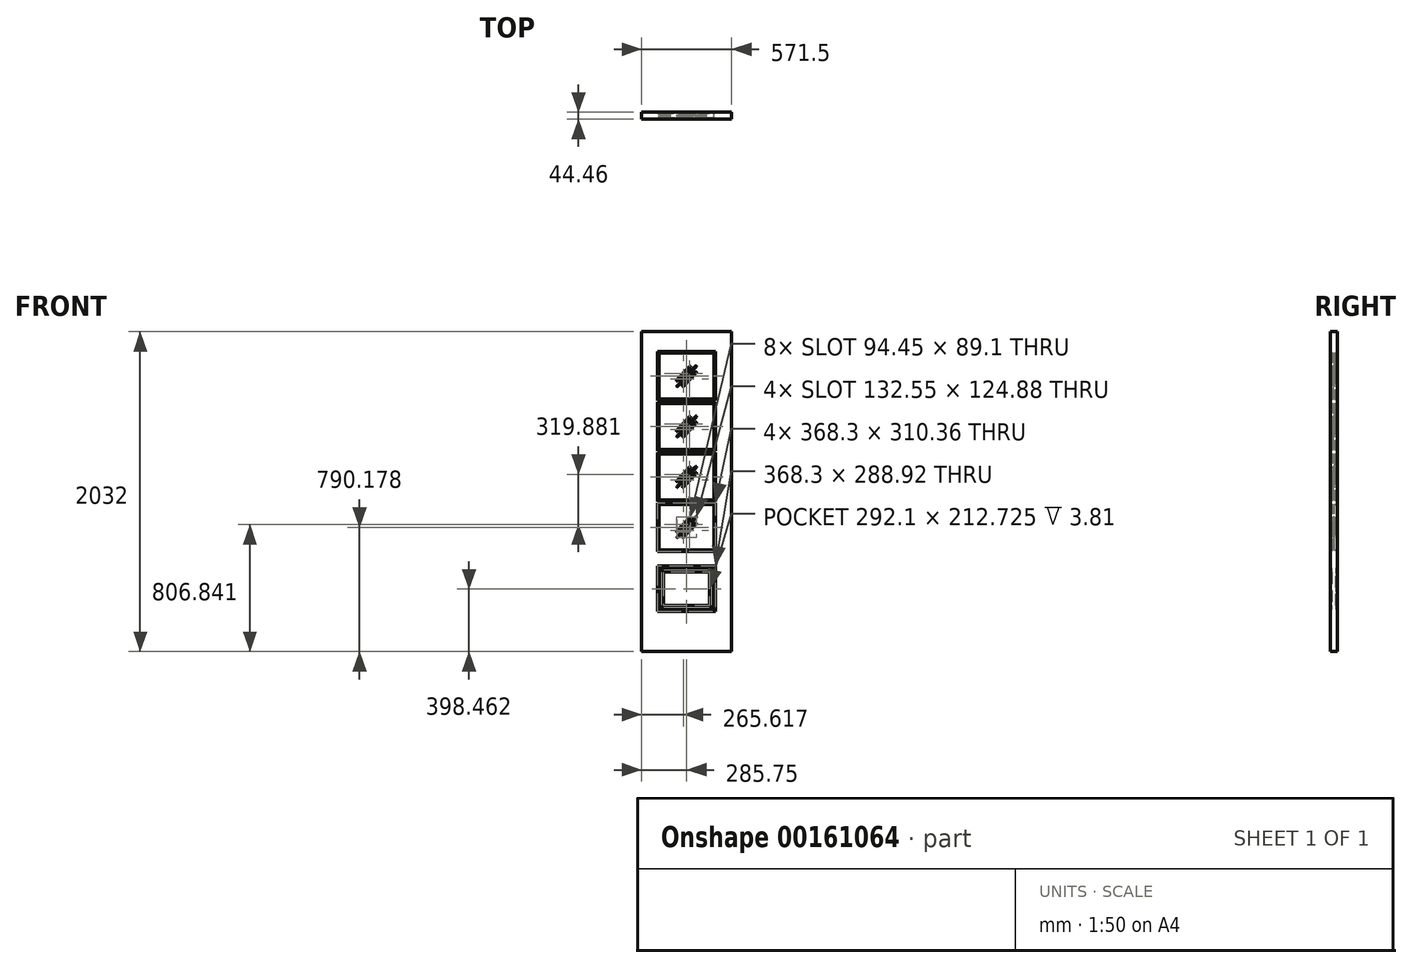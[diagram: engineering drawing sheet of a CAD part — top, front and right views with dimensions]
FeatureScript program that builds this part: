
annotation { "Feature Type Name" : "Feature", "Feature Type Description" : "" }
export const myFeature = defineFeature(function(context is Context, id is Id, definition is map)
    precondition{}
    {
        {
            var Q0;
            Q0=qCreatedBy(makeId("Front.planeOp"),FACE);
            var sketch = newSketch(context, id + "F0", { "sketchPlane" : qUnion([Q0])});
            skLineSegment(sketch, "E0.bottom", {"start": v(0, 2032) * mm, "end": v(571.5, 2032) * mm});
            skLineSegment(sketch, "E0.top", {"start": v(0, 0) * mm, "end": v(571.5, 0) * mm});
            skLineSegment(sketch, "E0.left", {"start": v(0, 2032) * mm, "end": v(0, 0) * mm});
            skLineSegment(sketch, "E0.right", {"start": v(571.5, 2032) * mm, "end": v(571.5, 0) * mm});
            skLineSegment(sketch, "E1.bottom", {"start": v(469.9, 254) * mm, "end": v(101.6, 254) * mm});
            skLineSegment(sketch, "E1.top", {"start": v(469.9, 542.93) * mm, "end": v(101.6, 542.93) * mm});
            skLineSegment(sketch, "E1.left", {"start": v(469.9, 254) * mm, "end": v(469.9, 542.93) * mm});
            skLineSegment(sketch, "E1.right", {"start": v(101.6, 254) * mm, "end": v(101.6, 542.93) * mm});
            skLineSegment(sketch, "E2.bottom", {"start": v(469.9, 635) * mm, "end": v(101.6, 635) * mm});
            skLineSegment(sketch, "E2.top", {"start": v(469.9, 945.36) * mm, "end": v(101.6, 945.36) * mm});
            skLineSegment(sketch, "E2.left", {"start": v(469.9, 635) * mm, "end": v(469.9, 945.36) * mm});
            skLineSegment(sketch, "E2.right", {"start": v(101.6, 635) * mm, "end": v(101.6, 945.36) * mm});
            skLineSegment(sketch, "E3.bottom", {"start": v(111.12, 935.83) * mm, "end": v(460.38, 935.83) * mm});
            skLineSegment(sketch, "E3.top", {"start": v(111.12, 644.53) * mm, "end": v(460.38, 644.53) * mm});
            skLineSegment(sketch, "E3.left", {"start": v(111.12, 935.83) * mm, "end": v(111.12, 644.53) * mm});
            skLineSegment(sketch, "E3.right", {"start": v(460.38, 935.83) * mm, "end": v(460.38, 644.53) * mm});
            skLineSegment(sketch, "E4", {"start": v(460.38, 935.83) * mm, "end": v(469.9, 945.36) * mm});
            skLineSegment(sketch, "E5", {"start": v(460.38, 644.53) * mm, "end": v(469.9, 635) * mm});
            skLineSegment(sketch, "E6", {"start": v(111.12, 644.52) * mm, "end": v(101.6, 635) * mm});
            skLineSegment(sketch, "E7", {"start": v(111.13, 935.83) * mm, "end": v(101.6, 945.36) * mm});
            skLineSegment(sketch, "E8", {"start": v(226.48, 727.08) * mm, "end": v(345.02, 853.28) * mm});
            skLineSegment(sketch, "E9", {"start": v(345.02, 815.18) * mm, "end": v(262.27, 727.08) * mm});
            skLineSegment(sketch, "E10.MirrorCS", {"start": v(307, 850.9) * mm, "end": v(224.24, 762.79) * mm});
            skLineSegment(sketch, "E11.0", {"start": v(457.2, 530.22) * mm, "end": v(114.3, 530.22) * mm});
            skLineSegment(sketch, "E11.1", {"start": v(457.2, 266.7) * mm, "end": v(457.2, 530.23) * mm});
            skLineSegment(sketch, "E11.2", {"start": v(457.2, 266.7) * mm, "end": v(114.3, 266.7) * mm});
            skLineSegment(sketch, "E11.3", {"start": v(114.3, 266.7) * mm, "end": v(114.3, 530.23) * mm});
            skLineSegment(sketch, "E12.0", {"start": v(431.8, 292.1) * mm, "end": v(139.7, 292.1) * mm});
            skLineSegment(sketch, "E12.1", {"start": v(431.8, 292.1) * mm, "end": v(431.8, 504.83) * mm});
            skLineSegment(sketch, "E12.2", {"start": v(431.8, 504.83) * mm, "end": v(139.7, 504.83) * mm});
            skLineSegment(sketch, "E12.3", {"start": v(139.7, 292.1) * mm, "end": v(139.7, 504.83) * mm});
            skLineSegment(sketch, "E13.0.1.0", {"start": v(307, 1170.78) * mm, "end": v(224.24, 1082.67) * mm});
            skLineSegment(sketch, "E13.0.1.1", {"start": v(345.02, 1135.06) * mm, "end": v(262.27, 1046.96) * mm});
            skLineSegment(sketch, "E13.0.1.2", {"start": v(469.9, 954.88) * mm, "end": v(469.9, 1265.24) * mm});
            skLineSegment(sketch, "E13.0.1.3", {"start": v(469.9, 1265.24) * mm, "end": v(101.6, 1265.24) * mm});
            skLineSegment(sketch, "E13.0.1.4", {"start": v(460.38, 1255.71) * mm, "end": v(460.38, 964.4) * mm});
            skLineSegment(sketch, "E13.0.1.6", {"start": v(111.12, 1255.71) * mm, "end": v(111.12, 964.4) * mm});
            skLineSegment(sketch, "E13.0.1.7", {"start": v(101.6, 954.88) * mm, "end": v(101.6, 1265.24) * mm});
            skLineSegment(sketch, "E13.0.1.8", {"start": v(111.12, 1255.71) * mm, "end": v(460.38, 1255.71) * mm});
            skLineSegment(sketch, "E13.0.1.9", {"start": v(226.48, 1046.96) * mm, "end": v(345.02, 1173.16) * mm});
            skLineSegment(sketch, "E13.0.1.10", {"start": v(111.12, 964.4) * mm, "end": v(460.38, 964.4) * mm});
            skLineSegment(sketch, "E13.0.1.11", {"start": v(469.9, 954.88) * mm, "end": v(101.6, 954.88) * mm});
            skLineSegment(sketch, "E13.0.1.15", {"start": v(111.13, 964.4) * mm, "end": v(101.6, 954.88) * mm});
            skLineSegment(sketch, "E13.0.1.16", {"start": v(460.38, 964.4) * mm, "end": v(469.9, 954.88) * mm});
            skLineSegment(sketch, "E13.0.1.17", {"start": v(111.12, 1255.71) * mm, "end": v(101.6, 1265.24) * mm});
            skLineSegment(sketch, "E13.0.1.18", {"start": v(460.38, 1255.71) * mm, "end": v(469.9, 1265.24) * mm});
            skLineSegment(sketch, "E13.0.2.0", {"start": v(307, 1490.66) * mm, "end": v(224.24, 1402.55) * mm});
            skLineSegment(sketch, "E13.0.2.1", {"start": v(345.02, 1454.94) * mm, "end": v(262.27, 1366.84) * mm});
            skLineSegment(sketch, "E13.0.2.2", {"start": v(469.9, 1274.76) * mm, "end": v(469.9, 1585.12) * mm});
            skLineSegment(sketch, "E13.0.2.3", {"start": v(469.9, 1585.12) * mm, "end": v(101.6, 1585.12) * mm});
            skLineSegment(sketch, "E13.0.2.4", {"start": v(460.38, 1575.6) * mm, "end": v(460.38, 1284.29) * mm});
            skLineSegment(sketch, "E13.0.2.6", {"start": v(111.12, 1575.6) * mm, "end": v(111.12, 1284.29) * mm});
            skLineSegment(sketch, "E13.0.2.7", {"start": v(101.6, 1274.76) * mm, "end": v(101.6, 1585.12) * mm});
            skLineSegment(sketch, "E13.0.2.8", {"start": v(111.12, 1575.6) * mm, "end": v(460.38, 1575.6) * mm});
            skLineSegment(sketch, "E13.0.2.9", {"start": v(226.48, 1366.84) * mm, "end": v(345.02, 1493.04) * mm});
            skLineSegment(sketch, "E13.0.2.10", {"start": v(111.12, 1284.29) * mm, "end": v(460.38, 1284.29) * mm});
            skLineSegment(sketch, "E13.0.2.11", {"start": v(469.9, 1274.76) * mm, "end": v(101.6, 1274.76) * mm});
            skLineSegment(sketch, "E13.0.2.15", {"start": v(111.13, 1284.29) * mm, "end": v(101.6, 1274.76) * mm});
            skLineSegment(sketch, "E13.0.2.16", {"start": v(460.37, 1284.29) * mm, "end": v(469.9, 1274.76) * mm});
            skLineSegment(sketch, "E13.0.2.17", {"start": v(111.12, 1575.6) * mm, "end": v(101.6, 1585.12) * mm});
            skLineSegment(sketch, "E13.0.2.18", {"start": v(460.38, 1575.6) * mm, "end": v(469.9, 1585.12) * mm});
            skLineSegment(sketch, "E13.0.3.0", {"start": v(307, 1810.54) * mm, "end": v(224.24, 1722.43) * mm});
            skLineSegment(sketch, "E13.0.3.1", {"start": v(345.02, 1774.82) * mm, "end": v(262.27, 1686.72) * mm});
            skLineSegment(sketch, "E13.0.3.2", {"start": v(469.9, 1594.64) * mm, "end": v(469.9, 1905) * mm});
            skLineSegment(sketch, "E13.0.3.3", {"start": v(469.9, 1905) * mm, "end": v(101.6, 1905) * mm});
            skLineSegment(sketch, "E13.0.3.4", {"start": v(460.38, 1895.48) * mm, "end": v(460.38, 1604.17) * mm});
            skLineSegment(sketch, "E13.0.3.6", {"start": v(111.12, 1895.48) * mm, "end": v(111.12, 1604.17) * mm});
            skLineSegment(sketch, "E13.0.3.7", {"start": v(101.6, 1594.64) * mm, "end": v(101.6, 1905) * mm});
            skLineSegment(sketch, "E13.0.3.8", {"start": v(111.13, 1895.48) * mm, "end": v(460.38, 1895.48) * mm});
            skLineSegment(sketch, "E13.0.3.9", {"start": v(226.48, 1686.72) * mm, "end": v(345.02, 1812.92) * mm});
            skLineSegment(sketch, "E13.0.3.10", {"start": v(111.12, 1604.17) * mm, "end": v(460.38, 1604.17) * mm});
            skLineSegment(sketch, "E13.0.3.11", {"start": v(469.9, 1594.64) * mm, "end": v(101.6, 1594.64) * mm});
            skLineSegment(sketch, "E13.0.3.15", {"start": v(111.13, 1604.17) * mm, "end": v(101.6, 1594.64) * mm});
            skLineSegment(sketch, "E13.0.3.16", {"start": v(460.37, 1604.17) * mm, "end": v(469.9, 1594.64) * mm});
            skLineSegment(sketch, "E13.0.3.17", {"start": v(111.12, 1895.47) * mm, "end": v(101.6, 1905) * mm});
            skLineSegment(sketch, "E13.0.3.18", {"start": v(460.38, 1895.47) * mm, "end": v(469.9, 1905) * mm});
            skLineSegment(sketch, "E13.direction1", {"start": v(101.6, 635) * mm, "end": v(127, 635) * mm, "construction": true});
            skLineSegment(sketch, "E13.direction2", {"start": v(101.6, 635) * mm, "end": v(101.6, 954.88) * mm, "construction": true});
            skSolve(sketch);
        }
        {
            var Q0;
            Q0=qCreatedBy(makeId("Front.planeOp"),FACE);
            var sketch = newSketch(context, id + "F1", { "sketchPlane" : qUnion([Q0])});
            skLineSegment(sketch, "E14.0.0", {"start": v(571.5, 2032) * mm, "end": v(0, 2032) * mm});
            skLineSegment(sketch, "E14.0.1", {"start": v(0, 2032) * mm, "end": v(0, 0) * mm});
            skLineSegment(sketch, "E14.0.2", {"start": v(0, 0) * mm, "end": v(571.5, 0) * mm});
            skLineSegment(sketch, "E14.0.3", {"start": v(571.5, 0) * mm, "end": v(571.5, 2032) * mm});
            skLineSegment(sketch, "E15.0", {"start": v(469.9, 1905) * mm, "end": v(101.6, 1905) * mm});
            skLineSegment(sketch, "E16.0", {"start": v(101.6, 1594.64) * mm, "end": v(101.6, 1905) * mm});
            skLineSegment(sketch, "E17.0", {"start": v(469.9, 1594.64) * mm, "end": v(101.6, 1594.64) * mm});
            skLineSegment(sketch, "E18.0", {"start": v(469.9, 1594.64) * mm, "end": v(469.9, 1905) * mm});
            skLineSegment(sketch, "E19.0", {"start": v(469.9, 1274.76) * mm, "end": v(469.9, 1585.12) * mm});
            skLineSegment(sketch, "E20.0", {"start": v(469.9, 1585.12) * mm, "end": v(101.6, 1585.12) * mm});
            skLineSegment(sketch, "E21.0", {"start": v(101.6, 1274.76) * mm, "end": v(101.6, 1585.12) * mm});
            skLineSegment(sketch, "E22.0", {"start": v(469.9, 1274.76) * mm, "end": v(101.6, 1274.76) * mm});
            skLineSegment(sketch, "E23.0", {"start": v(469.9, 1265.24) * mm, "end": v(101.6, 1265.24) * mm});
            skLineSegment(sketch, "E24.0", {"start": v(469.9, 954.88) * mm, "end": v(469.9, 1265.24) * mm});
            skLineSegment(sketch, "E25.0", {"start": v(101.6, 954.88) * mm, "end": v(101.6, 1265.24) * mm});
            skLineSegment(sketch, "E26.0", {"start": v(469.9, 954.88) * mm, "end": v(101.6, 954.88) * mm});
            skLineSegment(sketch, "E27.0", {"start": v(469.9, 945.36) * mm, "end": v(101.6, 945.36) * mm});
            skLineSegment(sketch, "E28.0", {"start": v(101.6, 635) * mm, "end": v(101.6, 945.36) * mm});
            skLineSegment(sketch, "E29.0", {"start": v(469.9, 635) * mm, "end": v(469.9, 945.36) * mm});
            skLineSegment(sketch, "E30.0", {"start": v(469.9, 635) * mm, "end": v(101.6, 635) * mm});
            skLineSegment(sketch, "E31.0", {"start": v(469.9, 542.93) * mm, "end": v(101.6, 542.93) * mm});
            skLineSegment(sketch, "E32.0", {"start": v(469.9, 254) * mm, "end": v(469.9, 542.93) * mm});
            skLineSegment(sketch, "E33.0", {"start": v(469.9, 254) * mm, "end": v(101.6, 254) * mm});
            skLineSegment(sketch, "E34.0", {"start": v(101.6, 254) * mm, "end": v(101.6, 542.93) * mm});
            skSolve(sketch);
        }
        {
            var Q0;
            Q0 = qSketchRegion(id + "F1", true);
            extrude(context, id + "F2", {"entities" : qUnion([Q0]), "depth" : 22.22 * mm, "hasSecondDirection" : true, "secondDirectionOppositeDirection" : true, "secondDirectionDepth" : 22.22 * mm});
        }
        {
            var Q0;
            Q0=qCreatedBy(makeId("Front.planeOp"),FACE);
            var sketch = newSketch(context, id + "F3", { "sketchPlane" : qUnion([Q0])});
            skLineSegment(sketch, "E35.0.0", {"start": v(460.38, 1895.47) * mm, "end": v(469.9, 1905) * mm});
            skLineSegment(sketch, "E35.0.1", {"start": v(469.9, 1905) * mm, "end": v(101.6, 1905) * mm});
            skLineSegment(sketch, "E35.0.2", {"start": v(101.6, 1905) * mm, "end": v(111.12, 1895.47) * mm});
            skLineSegment(sketch, "E35.0.3", {"start": v(111.12, 1895.48) * mm, "end": v(460.38, 1895.48) * mm});
            skLineSegment(sketch, "E36.0.0", {"start": v(460.37, 1604.17) * mm, "end": v(111.13, 1604.17) * mm});
            skLineSegment(sketch, "E36.0.1", {"start": v(111.13, 1604.17) * mm, "end": v(101.6, 1594.64) * mm});
            skLineSegment(sketch, "E36.0.2", {"start": v(101.6, 1594.64) * mm, "end": v(469.9, 1594.64) * mm});
            skLineSegment(sketch, "E36.0.3", {"start": v(469.9, 1594.64) * mm, "end": v(460.37, 1604.17) * mm});
            skLineSegment(sketch, "E37.0.0", {"start": v(460.38, 1575.6) * mm, "end": v(469.9, 1585.12) * mm});
            skLineSegment(sketch, "E37.0.1", {"start": v(469.9, 1585.12) * mm, "end": v(101.6, 1585.12) * mm});
            skLineSegment(sketch, "E37.0.2", {"start": v(101.6, 1585.12) * mm, "end": v(111.12, 1575.6) * mm});
            skLineSegment(sketch, "E37.0.3", {"start": v(111.12, 1575.6) * mm, "end": v(460.38, 1575.6) * mm});
            skLineSegment(sketch, "E38.0.0", {"start": v(460.37, 1284.29) * mm, "end": v(111.13, 1284.29) * mm});
            skLineSegment(sketch, "E38.0.1", {"start": v(111.13, 1284.29) * mm, "end": v(101.6, 1274.76) * mm});
            skLineSegment(sketch, "E38.0.2", {"start": v(101.6, 1274.76) * mm, "end": v(469.9, 1274.76) * mm});
            skLineSegment(sketch, "E38.0.3", {"start": v(469.9, 1274.76) * mm, "end": v(460.37, 1284.29) * mm});
            skLineSegment(sketch, "E39.0.0", {"start": v(460.38, 1255.71) * mm, "end": v(469.9, 1265.24) * mm});
            skLineSegment(sketch, "E39.0.1", {"start": v(469.9, 1265.24) * mm, "end": v(101.6, 1265.24) * mm});
            skLineSegment(sketch, "E39.0.2", {"start": v(101.6, 1265.24) * mm, "end": v(111.12, 1255.71) * mm});
            skLineSegment(sketch, "E39.0.3", {"start": v(111.12, 1255.71) * mm, "end": v(460.38, 1255.71) * mm});
            skLineSegment(sketch, "E40.0.0", {"start": v(460.38, 964.4) * mm, "end": v(111.12, 964.4) * mm});
            skLineSegment(sketch, "E40.0.1", {"start": v(111.13, 964.4) * mm, "end": v(101.6, 954.88) * mm});
            skLineSegment(sketch, "E40.0.2", {"start": v(101.6, 954.88) * mm, "end": v(469.9, 954.88) * mm});
            skLineSegment(sketch, "E40.0.3", {"start": v(469.9, 954.88) * mm, "end": v(460.38, 964.4) * mm});
            skLineSegment(sketch, "E41.0.0", {"start": v(460.38, 935.83) * mm, "end": v(469.9, 945.36) * mm});
            skLineSegment(sketch, "E41.0.1", {"start": v(469.9, 945.36) * mm, "end": v(101.6, 945.36) * mm});
            skLineSegment(sketch, "E41.0.2", {"start": v(101.6, 945.36) * mm, "end": v(111.13, 935.83) * mm});
            skLineSegment(sketch, "E41.0.3", {"start": v(111.12, 935.83) * mm, "end": v(460.38, 935.83) * mm});
            skLineSegment(sketch, "E42.0.0", {"start": v(101.6, 635) * mm, "end": v(469.9, 635) * mm});
            skLineSegment(sketch, "E42.0.1", {"start": v(469.9, 635) * mm, "end": v(460.38, 644.53) * mm});
            skLineSegment(sketch, "E42.0.2", {"start": v(460.38, 644.53) * mm, "end": v(111.12, 644.53) * mm});
            skLineSegment(sketch, "E42.0.3", {"start": v(111.12, 644.52) * mm, "end": v(101.6, 635) * mm});
            skLineSegment(sketch, "E43.0", {"start": v(469.9, 542.93) * mm, "end": v(101.6, 542.93) * mm});
            skLineSegment(sketch, "E44.0", {"start": v(469.9, 254) * mm, "end": v(101.6, 254) * mm});
            skLineSegment(sketch, "E45.0", {"start": v(457.2, 530.22) * mm, "end": v(114.3, 530.22) * mm});
            skLineSegment(sketch, "E46.0", {"start": v(457.2, 266.7) * mm, "end": v(114.3, 266.7) * mm});
            skLineSegment(sketch, "E47", {"start": v(114.3, 530.22) * mm, "end": v(101.6, 542.93) * mm});
            skLineSegment(sketch, "E48", {"start": v(457.2, 530.22) * mm, "end": v(469.9, 542.93) * mm});
            skLineSegment(sketch, "E49", {"start": v(457.2, 266.7) * mm, "end": v(469.9, 254) * mm});
            skLineSegment(sketch, "E50", {"start": v(114.3, 266.7) * mm, "end": v(101.6, 254) * mm});
            skSolve(sketch);
        }
        {
            var Q0;
            Q0 = qSketchRegion(id + "F3", true);
            extrude(context, id + "F4", {"entities" : qUnion([Q0]), "operationType" : NewBodyOperationType.ADD, "depth" : 20.02 * mm, "hasSecondDirection" : true, "secondDirectionOppositeDirection" : true, "secondDirectionDepth" : 20.02 * mm});
        }
        {
            var Q0;
            Q0=qCreatedBy(makeId("Front.planeOp"),FACE);
            var sketch = newSketch(context, id + "F5", { "sketchPlane" : qUnion([Q0])});
            skLineSegment(sketch, "E51.0.0", {"start": v(111.12, 1604.17) * mm, "end": v(111.12, 1895.47) * mm});
            skLineSegment(sketch, "E51.0.1", {"start": v(111.12, 1895.47) * mm, "end": v(101.6, 1905) * mm});
            skLineSegment(sketch, "E51.0.2", {"start": v(101.6, 1905) * mm, "end": v(101.6, 1594.64) * mm});
            skLineSegment(sketch, "E51.0.3", {"start": v(101.6, 1594.64) * mm, "end": v(111.13, 1604.17) * mm});
            skLineSegment(sketch, "E52.0.0", {"start": v(460.37, 1604.17) * mm, "end": v(469.9, 1594.64) * mm});
            skLineSegment(sketch, "E52.0.1", {"start": v(469.9, 1594.64) * mm, "end": v(469.9, 1905) * mm});
            skLineSegment(sketch, "E52.0.2", {"start": v(469.9, 1905) * mm, "end": v(460.38, 1895.47) * mm});
            skLineSegment(sketch, "E52.0.3", {"start": v(460.38, 1895.47) * mm, "end": v(460.38, 1604.17) * mm});
            skLineSegment(sketch, "E53.0.0", {"start": v(111.12, 1284.29) * mm, "end": v(111.12, 1575.6) * mm});
            skLineSegment(sketch, "E53.0.1", {"start": v(111.12, 1575.6) * mm, "end": v(101.6, 1585.12) * mm});
            skLineSegment(sketch, "E53.0.2", {"start": v(101.6, 1585.12) * mm, "end": v(101.6, 1274.76) * mm});
            skLineSegment(sketch, "E53.0.3", {"start": v(101.6, 1274.76) * mm, "end": v(111.13, 1284.29) * mm});
            skLineSegment(sketch, "E54.0.0", {"start": v(460.37, 1284.29) * mm, "end": v(469.9, 1274.76) * mm});
            skLineSegment(sketch, "E54.0.1", {"start": v(469.9, 1274.76) * mm, "end": v(469.9, 1585.12) * mm});
            skLineSegment(sketch, "E54.0.2", {"start": v(469.9, 1585.12) * mm, "end": v(460.38, 1575.6) * mm});
            skLineSegment(sketch, "E54.0.3", {"start": v(460.38, 1575.6) * mm, "end": v(460.38, 1284.29) * mm});
            skLineSegment(sketch, "E55.0.0", {"start": v(111.12, 964.4) * mm, "end": v(111.12, 1255.71) * mm});
            skLineSegment(sketch, "E55.0.1", {"start": v(111.12, 1255.71) * mm, "end": v(101.6, 1265.24) * mm});
            skLineSegment(sketch, "E55.0.2", {"start": v(101.6, 1265.24) * mm, "end": v(101.6, 954.88) * mm});
            skLineSegment(sketch, "E55.0.3", {"start": v(101.6, 954.88) * mm, "end": v(111.13, 964.4) * mm});
            skLineSegment(sketch, "E56.0.0", {"start": v(460.38, 964.4) * mm, "end": v(469.9, 954.88) * mm});
            skLineSegment(sketch, "E56.0.1", {"start": v(469.9, 954.88) * mm, "end": v(469.9, 1265.24) * mm});
            skLineSegment(sketch, "E56.0.2", {"start": v(469.9, 1265.24) * mm, "end": v(460.38, 1255.71) * mm});
            skLineSegment(sketch, "E56.0.3", {"start": v(460.38, 1255.71) * mm, "end": v(460.38, 964.4) * mm});
            skLineSegment(sketch, "E57.0.0", {"start": v(101.6, 945.36) * mm, "end": v(101.6, 635) * mm});
            skLineSegment(sketch, "E57.0.1", {"start": v(101.6, 635) * mm, "end": v(111.12, 644.52) * mm});
            skLineSegment(sketch, "E57.0.2", {"start": v(111.12, 644.53) * mm, "end": v(111.12, 935.83) * mm});
            skLineSegment(sketch, "E57.0.3", {"start": v(111.13, 935.83) * mm, "end": v(101.6, 945.36) * mm});
            skLineSegment(sketch, "E58.0.0", {"start": v(460.38, 644.53) * mm, "end": v(469.9, 635) * mm});
            skLineSegment(sketch, "E58.0.1", {"start": v(469.9, 635) * mm, "end": v(469.9, 945.36) * mm});
            skLineSegment(sketch, "E58.0.2", {"start": v(469.9, 945.36) * mm, "end": v(460.38, 935.83) * mm});
            skLineSegment(sketch, "E58.0.3", {"start": v(460.38, 935.83) * mm, "end": v(460.38, 644.53) * mm});
            skLineSegment(sketch, "E59.0", {"start": v(114.3, 266.7) * mm, "end": v(114.3, 530.23) * mm});
            skLineSegment(sketch, "E60.0", {"start": v(114.3, 530.22) * mm, "end": v(101.6, 542.93) * mm});
            skLineSegment(sketch, "E61.0", {"start": v(101.6, 254) * mm, "end": v(101.6, 542.93) * mm});
            skLineSegment(sketch, "E62.0", {"start": v(114.3, 266.7) * mm, "end": v(101.6, 254) * mm});
            skLineSegment(sketch, "E63.0", {"start": v(457.2, 266.7) * mm, "end": v(469.9, 254) * mm});
            skLineSegment(sketch, "E64.0", {"start": v(457.2, 266.7) * mm, "end": v(457.2, 530.23) * mm});
            skLineSegment(sketch, "E65.0", {"start": v(469.9, 254) * mm, "end": v(469.9, 542.93) * mm});
            skLineSegment(sketch, "E66.0", {"start": v(457.2, 530.22) * mm, "end": v(469.9, 542.93) * mm});
            skSolve(sketch);
        }
        {
            var Q0;
            Q0 = qSketchRegion(id + "F5", true);
            extrude(context, id + "F6", {"entities" : qUnion([Q0]), "operationType" : NewBodyOperationType.ADD, "depth" : 19.05 * mm, "hasSecondDirection" : true, "secondDirectionOppositeDirection" : true, "secondDirectionDepth" : 19.05 * mm});
        }
        {
            var Q0;
            Q0=qCreatedBy(makeId("Front.planeOp"),FACE);
            var sketch = newSketch(context, id + "F7", { "sketchPlane" : qUnion([Q0])});
            skLineSegment(sketch, "E67.0", {"start": v(457.2, 530.22) * mm, "end": v(114.3, 530.22) * mm});
            skLineSegment(sketch, "E68.0", {"start": v(431.8, 504.83) * mm, "end": v(139.7, 504.83) * mm});
            skLineSegment(sketch, "E69.0", {"start": v(431.8, 292.1) * mm, "end": v(139.7, 292.1) * mm});
            skLineSegment(sketch, "E70.0", {"start": v(457.2, 266.7) * mm, "end": v(114.3, 266.7) * mm});
            skLineSegment(sketch, "E71", {"start": v(114.3, 530.22) * mm, "end": v(139.7, 504.83) * mm});
            skLineSegment(sketch, "E72", {"start": v(431.8, 292.1) * mm, "end": v(457.2, 266.7) * mm});
            skLineSegment(sketch, "E73", {"start": v(457.2, 530.22) * mm, "end": v(431.8, 504.83) * mm});
            skLineSegment(sketch, "E74", {"start": v(139.7, 292.1) * mm, "end": v(114.3, 266.7) * mm});
            skSolve(sketch);
        }
        {
            var Q0;
            Q0 = qSketchRegion(id + "F7", true);
            extrude(context, id + "F8", {"entities" : qUnion([Q0]), "operationType" : NewBodyOperationType.ADD, "depth" : 17.78 * mm, "hasSecondDirection" : true, "secondDirectionOppositeDirection" : true, "secondDirectionDepth" : 17.78 * mm});
        }
        {
            var Q0;
            Q0=qCreatedBy(makeId("Front.planeOp"),FACE);
            var sketch = newSketch(context, id + "F9", { "sketchPlane" : qUnion([Q0])});
            skLineSegment(sketch, "E75.0", {"start": v(114.3, 530.22) * mm, "end": v(139.7, 504.83) * mm});
            skLineSegment(sketch, "E76.0", {"start": v(114.3, 266.7) * mm, "end": v(114.3, 530.23) * mm});
            skLineSegment(sketch, "E77.0", {"start": v(139.7, 292.1) * mm, "end": v(139.7, 504.83) * mm});
            skLineSegment(sketch, "E78.0", {"start": v(139.7, 292.1) * mm, "end": v(114.3, 266.7) * mm});
            skLineSegment(sketch, "E79.0", {"start": v(431.8, 292.1) * mm, "end": v(457.2, 266.7) * mm});
            skLineSegment(sketch, "E80.0", {"start": v(457.2, 530.22) * mm, "end": v(431.8, 504.83) * mm});
            skLineSegment(sketch, "E81.0", {"start": v(431.8, 292.1) * mm, "end": v(431.8, 504.83) * mm});
            skLineSegment(sketch, "E82.0", {"start": v(457.2, 266.7) * mm, "end": v(457.2, 530.23) * mm});
            skSolve(sketch);
        }
        {
            var Q0;
            Q0 = qSketchRegion(id + "F9", true);
            extrude(context, id + "F10", {"entities" : qUnion([Q0]), "operationType" : NewBodyOperationType.ADD, "depth" : 16.5 * mm, "hasSecondDirection" : true, "secondDirectionOppositeDirection" : true, "secondDirectionDepth" : 16.5 * mm});
        }
        {
            var Q0;
            Q0=qCreatedBy(makeId("Front.planeOp"),FACE);
            var sketch = newSketch(context, id + "F11", { "sketchPlane" : qUnion([Q0])});
            skLineSegment(sketch, "E83.0.0", {"start": v(139.7, 292.1) * mm, "end": v(431.8, 292.1) * mm});
            skLineSegment(sketch, "E83.0.1", {"start": v(431.8, 292.1) * mm, "end": v(431.8, 504.83) * mm});
            skLineSegment(sketch, "E83.0.2", {"start": v(431.8, 504.83) * mm, "end": v(139.7, 504.83) * mm});
            skLineSegment(sketch, "E83.0.3", {"start": v(139.7, 504.83) * mm, "end": v(139.7, 292.1) * mm});
            skSolve(sketch);
        }
        {
            var Q0;
            Q0 = qSketchRegion(id + "F11", true);
            extrude(context, id + "F12", {"entities" : qUnion([Q0]), "operationType" : NewBodyOperationType.ADD, "depth" : 12.7 * mm, "hasSecondDirection" : true, "secondDirectionOppositeDirection" : true, "secondDirectionDepth" : 12.7 * mm});
        }
        {
            var Q0;
            Q0=qCreatedBy(makeId("Front.planeOp"),FACE);
            var sketch = newSketch(context, id + "F13", { "sketchPlane" : qUnion([Q0])});
            skLineSegment(sketch, "E84.0.0", {"start": v(460.38, 1604.17) * mm, "end": v(460.38, 1895.47) * mm});
            skLineSegment(sketch, "E84.0.1", {"start": v(460.38, 1895.48) * mm, "end": v(111.12, 1895.48) * mm});
            skLineSegment(sketch, "E84.0.2", {"start": v(111.12, 1895.47) * mm, "end": v(111.12, 1604.17) * mm});
            skLineSegment(sketch, "E84.0.3", {"start": v(111.13, 1604.17) * mm, "end": v(460.37, 1604.17) * mm});
            skLineSegment(sketch, "E85.0.0", {"start": v(460.38, 1284.29) * mm, "end": v(460.38, 1575.6) * mm});
            skLineSegment(sketch, "E85.0.1", {"start": v(460.38, 1575.6) * mm, "end": v(111.12, 1575.6) * mm});
            skLineSegment(sketch, "E85.0.2", {"start": v(111.12, 1575.6) * mm, "end": v(111.12, 1284.29) * mm});
            skLineSegment(sketch, "E85.0.3", {"start": v(111.13, 1284.29) * mm, "end": v(460.37, 1284.29) * mm});
            skLineSegment(sketch, "E86.0.0", {"start": v(460.38, 964.4) * mm, "end": v(460.38, 1255.71) * mm});
            skLineSegment(sketch, "E86.0.1", {"start": v(460.38, 1255.71) * mm, "end": v(111.12, 1255.71) * mm});
            skLineSegment(sketch, "E86.0.2", {"start": v(111.12, 1255.71) * mm, "end": v(111.12, 964.4) * mm});
            skLineSegment(sketch, "E86.0.3", {"start": v(111.12, 964.4) * mm, "end": v(460.38, 964.4) * mm});
            skLineSegment(sketch, "E87.0.0", {"start": v(460.38, 935.83) * mm, "end": v(111.12, 935.83) * mm});
            skLineSegment(sketch, "E87.0.1", {"start": v(111.12, 935.83) * mm, "end": v(111.12, 644.53) * mm});
            skLineSegment(sketch, "E87.0.2", {"start": v(111.12, 644.53) * mm, "end": v(460.38, 644.53) * mm});
            skLineSegment(sketch, "E87.0.3", {"start": v(460.38, 644.53) * mm, "end": v(460.38, 935.83) * mm});
            skSolve(sketch);
        }
        {
            var Q0;
            Q0 = qSketchRegion(id + "F13", true);
            extrude(context, id + "F14", {"entities" : qUnion([Q0]), "operationType" : NewBodyOperationType.ADD, "depth" : 3.17 * mm, "hasSecondDirection" : true, "secondDirectionOppositeDirection" : true, "secondDirectionDepth" : 3.17 * mm});
        }
        {
            var Q0;
            Q0=qCreatedBy(makeId("Front.planeOp"),FACE);
            var sketch = newSketch(context, id + "F15", { "sketchPlane" : qUnion([Q0])});
            skLineSegment(sketch, "E88.0", {"start": v(307, 1810.54) * mm, "end": v(224.24, 1722.43) * mm});
            skLineSegment(sketch, "E89.0", {"start": v(226.48, 1686.72) * mm, "end": v(345.02, 1812.92) * mm});
            skLineSegment(sketch, "E90.0", {"start": v(345.02, 1774.82) * mm, "end": v(262.27, 1686.72) * mm});
            skLineSegment(sketch, "E91.0", {"start": v(307, 1490.66) * mm, "end": v(224.24, 1402.55) * mm});
            skLineSegment(sketch, "E92.0", {"start": v(226.48, 1366.84) * mm, "end": v(345.02, 1493.04) * mm});
            skLineSegment(sketch, "E93.0", {"start": v(345.02, 1454.94) * mm, "end": v(262.27, 1366.84) * mm});
            skLineSegment(sketch, "E94.0", {"start": v(307, 1170.78) * mm, "end": v(224.24, 1082.67) * mm});
            skLineSegment(sketch, "E95.0", {"start": v(226.48, 1046.96) * mm, "end": v(345.02, 1173.16) * mm});
            skLineSegment(sketch, "E96.0", {"start": v(345.02, 1135.06) * mm, "end": v(262.27, 1046.96) * mm});
            skLineSegment(sketch, "E97.0", {"start": v(307, 850.9) * mm, "end": v(224.24, 762.79) * mm});
            skLineSegment(sketch, "E98.0", {"start": v(226.48, 727.08) * mm, "end": v(345.02, 853.28) * mm});
            skLineSegment(sketch, "E99.0", {"start": v(345.02, 815.18) * mm, "end": v(262.27, 727.08) * mm});
            skArc(sketch, "E100.0.startCap", {"start": v(304.68, 1172.95) * mm, "mid": v(309.17, 1173.1) * mm, "end": v(309.3, 1168.6) * mm});
            skArc(sketch, "E100.0.endCap", {"start": v(226.56, 1080.5) * mm, "mid": v(222.07, 1080.36) * mm, "end": v(221.93, 1084.84) * mm});
            skLineSegment(sketch, "E100.0.left", {"start": v(309.3, 1168.6) * mm, "end": v(226.56, 1080.5) * mm});
            skLineSegment(sketch, "E100.0.right", {"start": v(304.68, 1172.95) * mm, "end": v(221.93, 1084.84) * mm});
            skArc(sketch, "E100.1.startCap", {"start": v(228.8, 1044.78) * mm, "mid": v(224.3, 1044.64) * mm, "end": v(224.17, 1049.13) * mm});
            skArc(sketch, "E100.1.endCap", {"start": v(342.7, 1175.34) * mm, "mid": v(347.2, 1175.48) * mm, "end": v(347.33, 1170.99) * mm});
            skLineSegment(sketch, "E100.1.left", {"start": v(224.17, 1049.13) * mm, "end": v(342.7, 1175.34) * mm});
            skLineSegment(sketch, "E100.1.right", {"start": v(228.8, 1044.78) * mm, "end": v(347.33, 1170.99) * mm});
            skArc(sketch, "E100.2.startCap", {"start": v(228.8, 724.9) * mm, "mid": v(224.3, 724.76) * mm, "end": v(224.17, 729.25) * mm});
            skArc(sketch, "E100.2.endCap", {"start": v(342.7, 855.45) * mm, "mid": v(347.2, 855.6) * mm, "end": v(347.33, 851.1) * mm});
            skLineSegment(sketch, "E100.2.left", {"start": v(224.17, 729.25) * mm, "end": v(342.7, 855.45) * mm});
            skLineSegment(sketch, "E100.2.right", {"start": v(228.8, 724.9) * mm, "end": v(347.33, 851.1) * mm});
            skArc(sketch, "E100.3.startCap", {"start": v(304.68, 853.07) * mm, "mid": v(309.17, 853.2) * mm, "end": v(309.3, 848.72) * mm});
            skArc(sketch, "E100.3.endCap", {"start": v(226.56, 760.61) * mm, "mid": v(222.07, 760.47) * mm, "end": v(221.93, 764.96) * mm});
            skLineSegment(sketch, "E100.3.left", {"start": v(309.3, 848.72) * mm, "end": v(226.56, 760.61) * mm});
            skLineSegment(sketch, "E100.3.right", {"start": v(304.68, 853.07) * mm, "end": v(221.93, 764.96) * mm});
            skArc(sketch, "E100.4.startCap", {"start": v(342.7, 1457.12) * mm, "mid": v(347.2, 1457.26) * mm, "end": v(347.33, 1452.77) * mm});
            skArc(sketch, "E100.4.endCap", {"start": v(264.58, 1364.66) * mm, "mid": v(260.1, 1364.52) * mm, "end": v(259.95, 1369.01) * mm});
            skLineSegment(sketch, "E100.4.left", {"start": v(347.33, 1452.77) * mm, "end": v(264.58, 1364.66) * mm});
            skLineSegment(sketch, "E100.4.right", {"start": v(342.7, 1457.12) * mm, "end": v(259.95, 1369.01) * mm});
            skArc(sketch, "E100.5.startCap", {"start": v(342.7, 1137.24) * mm, "mid": v(347.2, 1137.38) * mm, "end": v(347.33, 1132.89) * mm});
            skArc(sketch, "E100.5.endCap", {"start": v(264.58, 1044.78) * mm, "mid": v(260.1, 1044.64) * mm, "end": v(259.95, 1049.13) * mm});
            skLineSegment(sketch, "E100.5.left", {"start": v(347.33, 1132.89) * mm, "end": v(264.58, 1044.78) * mm});
            skLineSegment(sketch, "E100.5.right", {"start": v(342.7, 1137.24) * mm, "end": v(259.95, 1049.13) * mm});
            skArc(sketch, "E100.6.startCap", {"start": v(228.8, 1364.66) * mm, "mid": v(224.3, 1364.52) * mm, "end": v(224.17, 1369.01) * mm});
            skArc(sketch, "E100.6.endCap", {"start": v(342.7, 1495.22) * mm, "mid": v(347.2, 1495.36) * mm, "end": v(347.33, 1490.87) * mm});
            skLineSegment(sketch, "E100.6.left", {"start": v(224.17, 1369.01) * mm, "end": v(342.7, 1495.22) * mm});
            skLineSegment(sketch, "E100.6.right", {"start": v(228.8, 1364.66) * mm, "end": v(347.33, 1490.87) * mm});
            skArc(sketch, "E100.7.startCap", {"start": v(304.68, 1492.83) * mm, "mid": v(309.17, 1492.97) * mm, "end": v(309.3, 1488.48) * mm});
            skArc(sketch, "E100.7.endCap", {"start": v(226.56, 1400.38) * mm, "mid": v(222.07, 1400.24) * mm, "end": v(221.93, 1404.72) * mm});
            skLineSegment(sketch, "E100.7.left", {"start": v(309.3, 1488.48) * mm, "end": v(226.56, 1400.38) * mm});
            skLineSegment(sketch, "E100.7.right", {"start": v(304.68, 1492.83) * mm, "end": v(221.93, 1404.72) * mm});
            skArc(sketch, "E100.8.startCap", {"start": v(342.7, 1777) * mm, "mid": v(347.2, 1777.14) * mm, "end": v(347.33, 1772.65) * mm});
            skArc(sketch, "E100.8.endCap", {"start": v(264.58, 1684.55) * mm, "mid": v(260.1, 1684.4) * mm, "end": v(259.95, 1688.9) * mm});
            skLineSegment(sketch, "E100.8.left", {"start": v(347.33, 1772.65) * mm, "end": v(264.58, 1684.55) * mm});
            skLineSegment(sketch, "E100.8.right", {"start": v(342.7, 1777) * mm, "end": v(259.95, 1688.9) * mm});
            skArc(sketch, "E100.9.startCap", {"start": v(228.8, 1684.55) * mm, "mid": v(224.3, 1684.4) * mm, "end": v(224.17, 1688.9) * mm});
            skArc(sketch, "E100.9.endCap", {"start": v(342.7, 1815.1) * mm, "mid": v(347.2, 1815.24) * mm, "end": v(347.33, 1810.75) * mm});
            skLineSegment(sketch, "E100.9.left", {"start": v(224.17, 1688.9) * mm, "end": v(342.7, 1815.1) * mm});
            skLineSegment(sketch, "E100.9.right", {"start": v(228.8, 1684.55) * mm, "end": v(347.33, 1810.75) * mm});
            skArc(sketch, "E100.10.startCap", {"start": v(342.7, 817.35) * mm, "mid": v(347.2, 817.5) * mm, "end": v(347.33, 813) * mm});
            skArc(sketch, "E100.10.endCap", {"start": v(264.58, 724.9) * mm, "mid": v(260.1, 724.76) * mm, "end": v(259.95, 729.25) * mm});
            skLineSegment(sketch, "E100.10.left", {"start": v(347.33, 813) * mm, "end": v(264.58, 724.9) * mm});
            skLineSegment(sketch, "E100.10.right", {"start": v(342.7, 817.35) * mm, "end": v(259.95, 729.25) * mm});
            skArc(sketch, "E100.11.startCap", {"start": v(304.68, 1812.71) * mm, "mid": v(309.17, 1812.85) * mm, "end": v(309.3, 1808.36) * mm});
            skArc(sketch, "E100.11.endCap", {"start": v(226.56, 1720.26) * mm, "mid": v(222.07, 1720.12) * mm, "end": v(221.93, 1724.6) * mm});
            skLineSegment(sketch, "E100.11.left", {"start": v(309.3, 1808.36) * mm, "end": v(226.56, 1720.26) * mm});
            skLineSegment(sketch, "E100.11.right", {"start": v(304.68, 1812.71) * mm, "end": v(221.93, 1724.6) * mm});
            skSolve(sketch);
        }
        {
            var Q0;
            Q0 = qSketchRegion(id + "F15", true);
            extrude(context, id + "F16", {"entities" : qUnion([Q0]), "operationType" : NewBodyOperationType.REMOVE, "oppositeDirection" : true, "depth" : 25.4 * mm, "hasSecondDirection" : true, "secondDirectionOppositeDirection" : false, "secondDirectionDepth" : 25.4 * mm});
        }
    });
